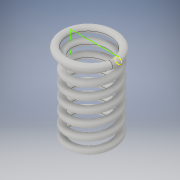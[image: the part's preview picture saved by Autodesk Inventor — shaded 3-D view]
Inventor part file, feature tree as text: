
AUTODESK INVENTOR PART (.ipt)
format: ipt  version: 2018 (Build 220112000, 112)  size: 635,904 bytes
history: native  units: in
note: dims shown in document units (in); Inventor stores cm internally (conversion verified against a paired STEP export)
features: sketch x3, helix x2, projected_geometry x2
ambient origin geometry x8: Origin, YZ Plane, XZ Plane, XY Plane, X Axis, Y Axis, Z Axis, Center Point
bodies: Solid1 (feature_tree)
feature tree (7):
  helix  "Coil1"  [1 undecoded]
  helix  "Coil2"  [1 undecoded]
  sketch  "Sketch6"
  sketch  "Sketch1"  dims[d2=1.0in d3=0.2146in d4=2.3622in d5=0.0in d6=90.0deg d7=0.481in d8=0.0in d9=0.0in]
  sketch  "Sketch2"  dims[d10=1.0in d11=0.016in d12=0.315in d13=0.3436in d14=0.0in d15=0.0in d16=75.0deg d17=0.0in]
  projected_geometry  "Projected Loop3"
  projected_geometry  "Projected Loop4"
note: 2 required parameter values undecoded (feature->parameter linkage not recoverable at this tier; creation-order binding heuristic only, values carry confidence <= 0.55)
